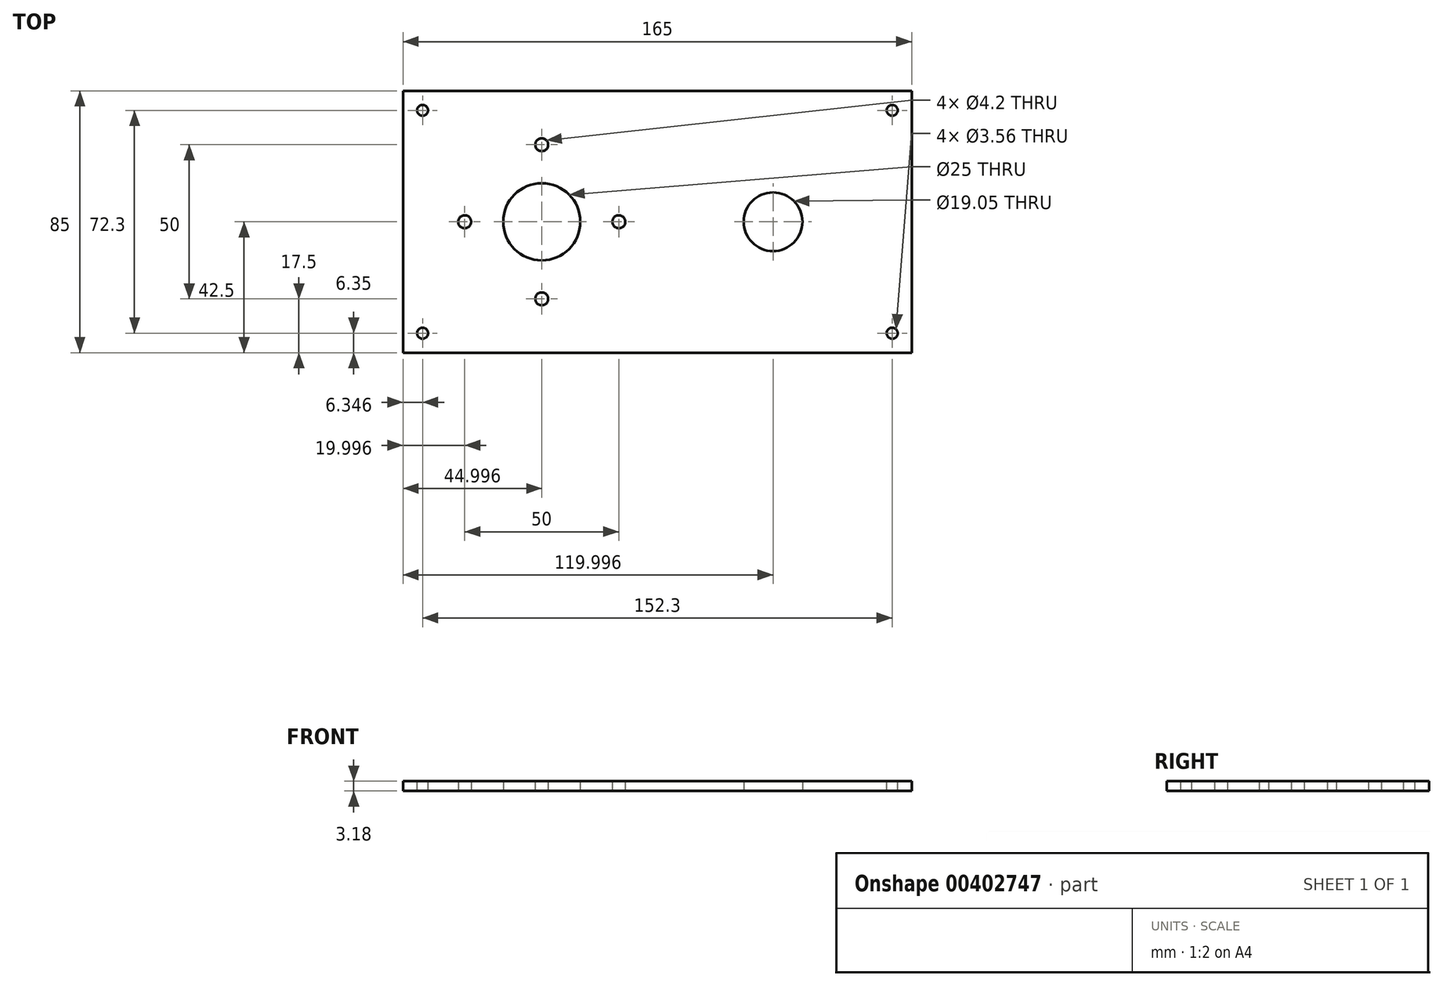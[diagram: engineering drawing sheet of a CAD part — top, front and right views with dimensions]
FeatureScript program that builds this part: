
annotation { "Feature Type Name" : "Feature", "Feature Type Description" : "" }
export const myFeature = defineFeature(function(context is Context, id is Id, definition is map)
    precondition{}
    {
        {
            var Q0;
            Q0=qCreatedBy(makeId("Top.planeOp"),FACE);
            var sketch = newSketch(context, id + "F0", { "sketchPlane" : qUnion([Q0])});
            skLineSegment(sketch, "E0.bottom", {"start": v(114.43, 44.74) * mm, "end": v(-50.57, 44.74) * mm});
            skLineSegment(sketch, "E0.top", {"start": v(114.43, -40.26) * mm, "end": v(-50.57, -40.26) * mm});
            skLineSegment(sketch, "E0.left", {"start": v(114.43, 44.74) * mm, "end": v(114.43, -40.26) * mm});
            skLineSegment(sketch, "E0.right", {"start": v(-50.57, 44.74) * mm, "end": v(-50.57, -40.26) * mm});
            skCircle(sketch, "E1", {"center": v(-5.57, 2.24) * mm, "radius": 12.5 * mm});
            skLineSegment(sketch, "E2", {"start": v(-5.57, 2.24) * mm, "end": v(-5.57, -22.76) * mm, "construction": true});
            skCircle(sketch, "E3", {"center": v(-5.57, -22.76) * mm, "radius": 2.1 * mm});
            skCircle(sketch, "E4.1.0", {"center": v(19.43, 2.24) * mm, "radius": 2.1 * mm});
            skCircle(sketch, "E4.2.0", {"center": v(-5.57, 27.24) * mm, "radius": 2.1 * mm});
            skCircle(sketch, "E4.3.0", {"center": v(-30.57, 2.24) * mm, "radius": 2.1 * mm});
            skLineSegment(sketch, "E5", {"start": v(114.43, 2.24) * mm, "end": v(-50.57, 2.24) * mm, "construction": true});
            skCircle(sketch, "E6", {"center": v(69.43, 2.24) * mm, "radius": 9.53 * mm});
            skLineSegment(sketch, "E7.0", {"start": v(104.43, 34.74) * mm, "end": v(-40.57, 34.74) * mm, "construction": true});
            skLineSegment(sketch, "E7.1", {"start": v(104.43, 34.74) * mm, "end": v(104.43, -30.26) * mm, "construction": true});
            skLineSegment(sketch, "E7.2", {"start": v(104.43, -30.26) * mm, "end": v(-40.57, -30.26) * mm, "construction": true});
            skLineSegment(sketch, "E7.3", {"start": v(-40.57, 34.74) * mm, "end": v(-40.57, -30.26) * mm, "construction": true});
            skSolve(sketch);
        }
        {
            var Q0;
            Q0=makeQuery(id+"F0.imprint","IMPRINT",FACE,{"disambiguationData":[TD([[makeQuery(id+"F0.imprint","IMPRINT",EDGE,{"derivedFrom":sQuery(id+"F0.wireOp",EDGE,"E0.bottom")}),1.0]])]});
            extrude(context, id + "F1", {"entities" : qUnion([Q0]), "depth" : 3.17 * mm});
        }
        {
            var Q0;
            Q0=makeQuery(id+"F1.opExtrude","CAP_FACE",FACE,{"disambiguationData":[OSD([sQuery(id+"F0.wireOp",EDGE,"E0.bottom"),sQuery(id+"F0.wireOp",EDGE,"E0.top"),sQuery(id+"F0.wireOp",EDGE,"E0.left"),sQuery(id+"F0.wireOp",EDGE,"E0.right"),sQuery(id+"F0.wireOp",EDGE,"E1"),sQuery(id+"F0.wireOp",EDGE,"E3"),sQuery(id+"F0.wireOp",EDGE,"E4.1.0"),sQuery(id+"F0.wireOp",EDGE,"E4.2.0"),sQuery(id+"F0.wireOp",EDGE,"E4.3.0"),sQuery(id+"F0.wireOp",EDGE,"E6")])],"isStart":false});
            var sketch = newSketch(context, id + "F2", { "sketchPlane" : qUnion([Q0])});
            skCircle(sketch, "E8", {"center": v(-44.22, 38.4) * mm, "radius": 1.78 * mm});
            skLineSegment(sketch, "E9", {"start": v(114.43, 2.24) * mm, "end": v(-50.57, 2.24) * mm, "construction": true});
            skCircle(sketch, "E10.MirrorC", {"center": v(-44.22, -33.9) * mm, "radius": 1.78 * mm});
            skLineSegment(sketch, "E11", {"start": v(31.93, 44.74) * mm, "end": v(31.93, -40.26) * mm, "construction": true});
            skCircle(sketch, "E12.MirrorC", {"center": v(108.08, 38.4) * mm, "radius": 1.78 * mm});
            skCircle(sketch, "E13.MirrorC", {"center": v(108.08, -33.9) * mm, "radius": 1.78 * mm});
            skSolve(sketch);
        }
        {
            var Q0;
            Q0 = qSketchRegion(id + "F2", true);
            extrude(context, id + "F3", {"entities" : qUnion([Q0]), "operationType" : NewBodyOperationType.REMOVE, "endBound" : BoundingType.UP_TO_NEXT, "oppositeDirection" : true, "depth" : 25 * mm});
        }
    });
